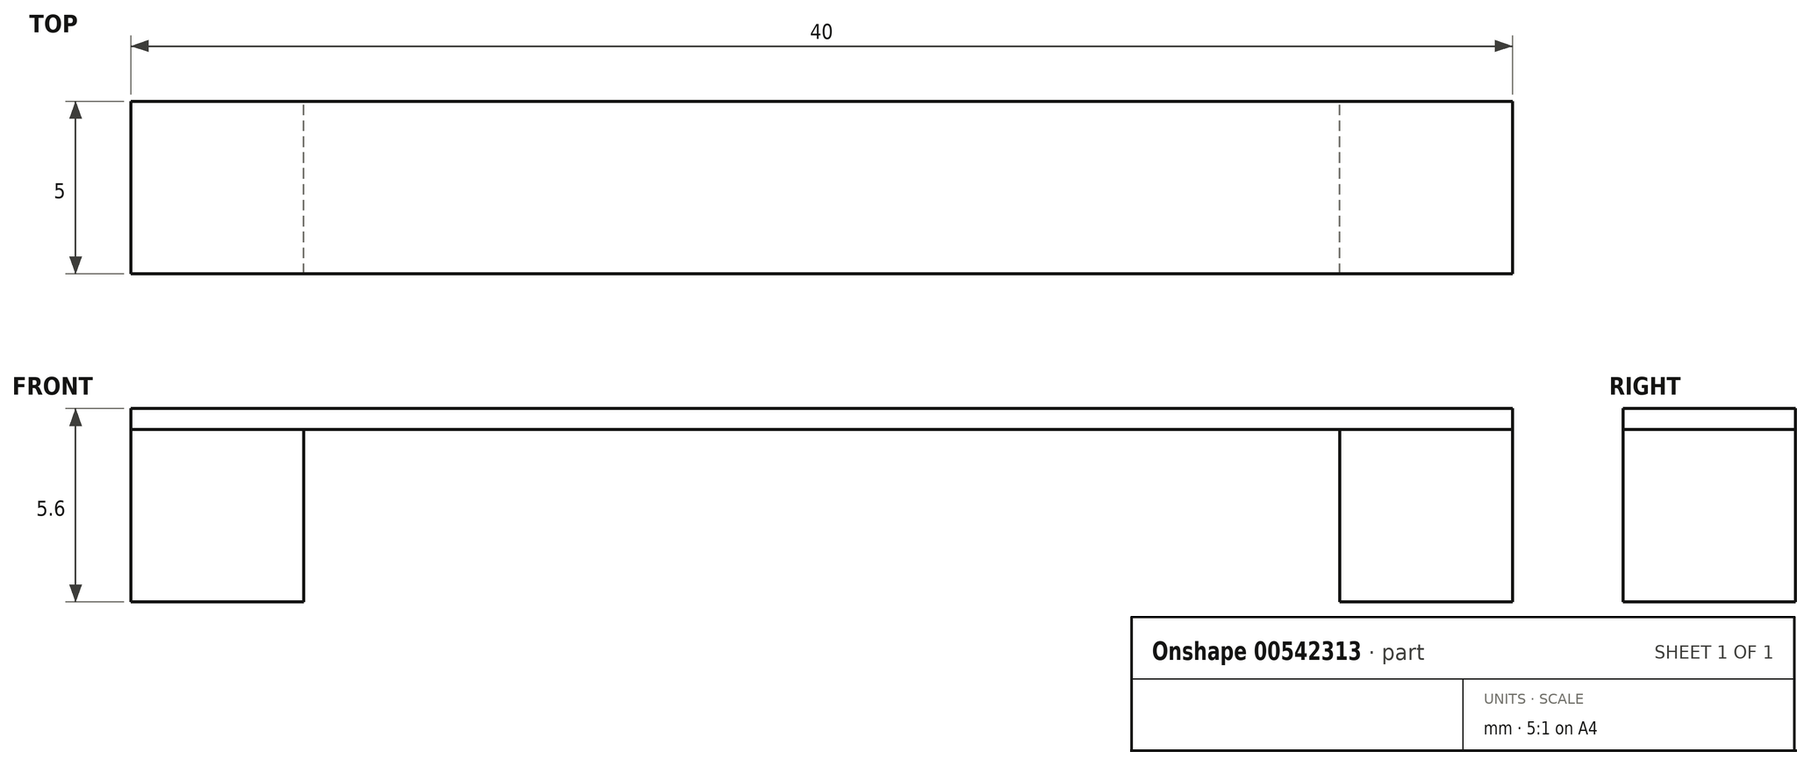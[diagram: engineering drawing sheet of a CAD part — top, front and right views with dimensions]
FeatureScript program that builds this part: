
annotation { "Feature Type Name" : "Feature", "Feature Type Description" : "" }
export const myFeature = defineFeature(function(context is Context, id is Id, definition is map)
    precondition{}
    {
        {
            var Q0;
            Q0=qCreatedBy(makeId("Top.planeOp"),FACE);
            var sketch = newSketch(context, id + "F0", { "sketchPlane" : qUnion([Q0])});
            skLineSegment(sketch, "E0.bottom", {"start": v(-20, 0) * mm, "end": v(-15, 0) * mm});
            skLineSegment(sketch, "E0.top", {"start": v(-20, 5) * mm, "end": v(-15, 5) * mm});
            skLineSegment(sketch, "E0.left", {"start": v(-20, 0) * mm, "end": v(-20, 5) * mm});
            skLineSegment(sketch, "E0.right", {"start": v(-15, 0) * mm, "end": v(-15, 5) * mm});
            skLineSegment(sketch, "E1.MirrorCS", {"start": v(15, 0) * mm, "end": v(15, 5) * mm});
            skLineSegment(sketch, "E2.MirrorCS", {"start": v(20, 0) * mm, "end": v(15, 0) * mm});
            skLineSegment(sketch, "E3.MirrorCS", {"start": v(20, 0) * mm, "end": v(20, 5) * mm});
            skLineSegment(sketch, "E4.MirrorCS", {"start": v(20, 5) * mm, "end": v(15, 5) * mm});
            skSolve(sketch);
        }
        {
            var Q0;
            Q0 = qSketchRegion(id + "F0", true);
            extrude(context, id + "F1", {"entities" : qUnion([Q0]), "depth" : 5 * mm, "offsetDistance" : 25 * mm});
        }
        {
            var Q0;
            Q0=makeQuery(id+"F1.opExtrude","SWEPT_FACE",FACE,{"disambiguationData":[OSD([sQuery(id+"F0.wireOp",EDGE,"E0.left")])]});
            var sketch = newSketch(context, id + "F2", { "sketchPlane" : qUnion([Q0])});
            skLineSegment(sketch, "E5.bottom", {"start": v(-5, 5) * mm, "end": v(0, 5) * mm});
            skLineSegment(sketch, "E5.top", {"start": v(-5, 5.6) * mm, "end": v(0, 5.6) * mm});
            skLineSegment(sketch, "E5.left", {"start": v(-5, 5) * mm, "end": v(-5, 5.6) * mm});
            skLineSegment(sketch, "E5.right", {"start": v(0, 5) * mm, "end": v(0, 5.6) * mm});
            skSolve(sketch);
        }
        {
            var Q0;
            Q0 = qSketchRegion(id + "F2", true);
            extrude(context, id + "F3", {"entities" : qUnion([Q0]), "oppositeDirection" : true, "depth" : 40 * mm, "offsetDistance" : 25 * mm});
        }
    });
